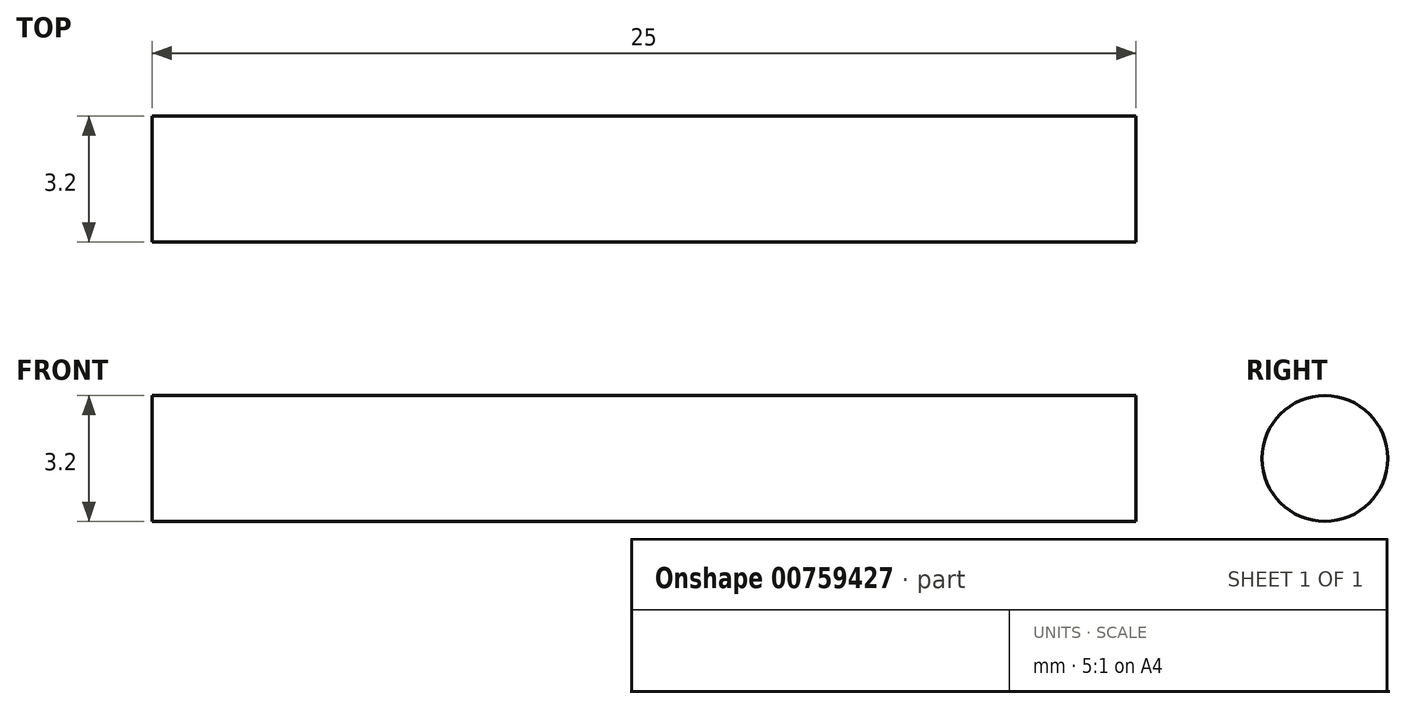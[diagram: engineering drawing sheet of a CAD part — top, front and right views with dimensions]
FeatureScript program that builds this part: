
annotation { "Feature Type Name" : "Feature", "Feature Type Description" : "" }
export const myFeature = defineFeature(function(context is Context, id is Id, definition is map)
    precondition{}
    {
        {
            var Q0;
            Q0=qCreatedBy(makeId("Right.planeOp"),FACE);
            var sketch = newSketch(context, id + "F0", { "sketchPlane" : qUnion([Q0])});
            skCircle(sketch, "E0", {"center": v(0, 0) * mm, "radius": 1.6 * mm});
            skSolve(sketch);
        }
        {
            var Q0;
            Q0 = qSketchRegion(id + "F0", true);
            extrude(context, id + "F1", {"entities" : qUnion([Q0]), "endBound" : BoundingType.SYMMETRIC, "depth" : 25 * mm, "offsetDistance" : 25 * mm});
        }
    });
